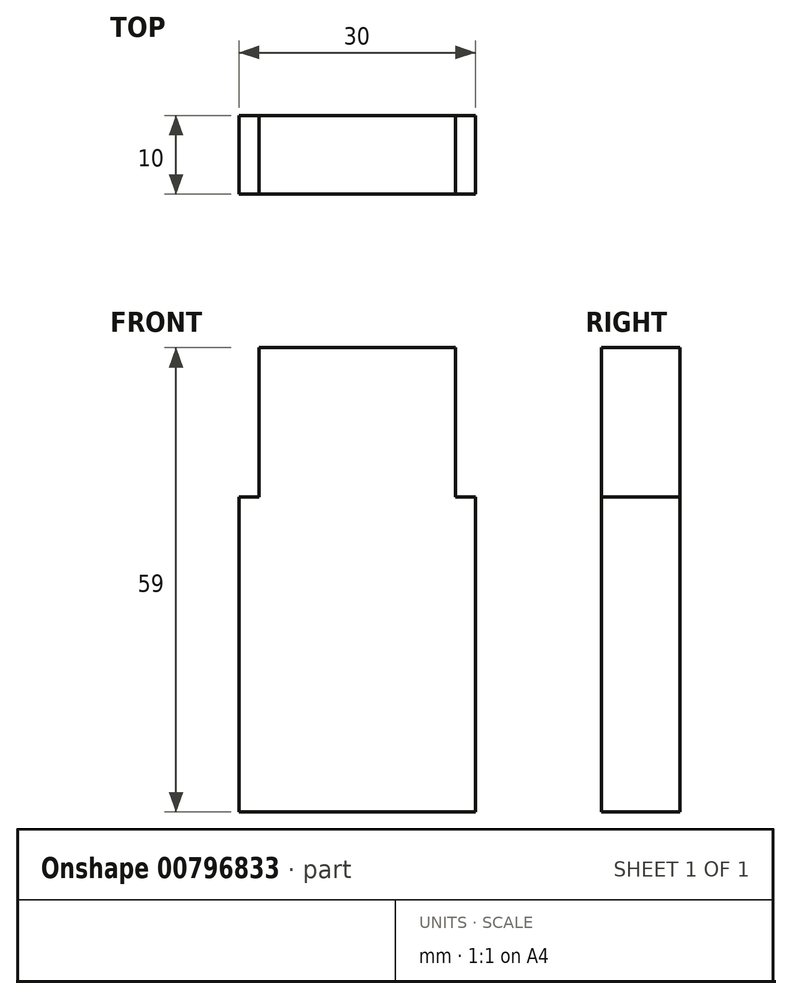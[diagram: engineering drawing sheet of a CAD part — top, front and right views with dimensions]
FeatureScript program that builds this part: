
annotation { "Feature Type Name" : "Feature", "Feature Type Description" : "" }
export const myFeature = defineFeature(function(context is Context, id is Id, definition is map)
    precondition{}
    {
        {
            var Q0;
            Q0=qCreatedBy(makeId("Top.planeOp"),FACE);
            var sketch = newSketch(context, id + "F0", { "sketchPlane" : qUnion([Q0])});
            skLineSegment(sketch, "E0.bottom", {"start": v(15, -5) * mm, "end": v(-15, -5) * mm});
            skLineSegment(sketch, "E0.top", {"start": v(15, 5) * mm, "end": v(-15, 5) * mm});
            skLineSegment(sketch, "E0.left", {"start": v(15, -5) * mm, "end": v(15, 5) * mm});
            skLineSegment(sketch, "E0.right", {"start": v(-15, -5) * mm, "end": v(-15, 5) * mm});
            skPoint(sketch, "E0.middle", {"position": v(0, 0) * mm});
            skSolve(sketch);
        }
        {
            var Q0;
            Q0=makeQuery(id+"F0.imprint","IMPRINT",FACE,{"disambiguationData":[TD([[makeQuery(id+"F0.imprint","IMPRINT",EDGE,{"derivedFrom":sQuery(id+"F0.wireOp",EDGE,"E0.bottom")}),-1.0]])]});
            extrude(context, id + "F1", {"entities" : qUnion([Q0]), "depth" : 40 * mm, "offsetDistance" : 25 * mm});
        }
        {
            var Q0;
            Q0=makeQuery(id+"F1.opExtrude","CAP_FACE",FACE,{"disambiguationData":[OSD([sQuery(id+"F0.wireOp",EDGE,"E0.bottom"),sQuery(id+"F0.wireOp",EDGE,"E0.top"),sQuery(id+"F0.wireOp",EDGE,"E0.left"),sQuery(id+"F0.wireOp",EDGE,"E0.right")])],"isStart":false});
            var sketch = newSketch(context, id + "F2", { "sketchPlane" : qUnion([Q0])});
            skLineSegment(sketch, "E1.bottom", {"start": v(12.5, -5) * mm, "end": v(-12.5, -5) * mm});
            skLineSegment(sketch, "E1.top", {"start": v(12.5, 5) * mm, "end": v(-12.5, 5) * mm});
            skLineSegment(sketch, "E1.left", {"start": v(12.5, -5) * mm, "end": v(12.5, 5) * mm});
            skLineSegment(sketch, "E1.right", {"start": v(-12.5, -5) * mm, "end": v(-12.5, 5) * mm});
            skPoint(sketch, "E1.middle", {"position": v(0, 0) * mm});
            skSolve(sketch);
        }
        {
            var Q0;
            Q0=makeQuery(id+"F2.imprint","IMPRINT",FACE,{"disambiguationData":[TD([[makeQuery(id+"F2.imprint","IMPRINT",EDGE,{"derivedFrom":sQuery(id+"F2.wireOp",EDGE,"E1.bottom")}),-1.0]])]});
            extrude(context, id + "F3", {"entities" : qUnion([Q0]), "operationType" : NewBodyOperationType.ADD, "depth" : 12 * mm, "offsetDistance" : 25 * mm});
        }
        {
            var Q0;
            Q0=makeQuery(id+"F3.opExtrude","CAP_FACE",FACE,{"disambiguationData":[OSD([sQuery(id+"F2.wireOp",EDGE,"E1.bottom"),sQuery(id+"F2.wireOp",EDGE,"E1.top"),sQuery(id+"F2.wireOp",EDGE,"E1.left"),sQuery(id+"F2.wireOp",EDGE,"E1.right")])],"isStart":false});
            var sketch = newSketch(context, id + "F4", { "sketchPlane" : qUnion([Q0])});
            skLineSegment(sketch, "E2.bottom", {"start": v(12.5, -5) * mm, "end": v(-12.5, -5) * mm});
            skLineSegment(sketch, "E2.top", {"start": v(12.5, 5) * mm, "end": v(-12.5, 5) * mm});
            skLineSegment(sketch, "E2.left", {"start": v(12.5, -5) * mm, "end": v(12.5, 5) * mm});
            skLineSegment(sketch, "E2.right", {"start": v(-12.5, -5) * mm, "end": v(-12.5, 5) * mm});
            skPoint(sketch, "E2.middle", {"position": v(0, 0) * mm});
            skSolve(sketch);
        }
        {
            var Q0;
            Q0=makeQuery(id+"F4.imprint","IMPRINT",FACE,{"disambiguationData":[TD([[makeQuery(id+"F4.imprint","IMPRINT",EDGE,{"derivedFrom":sQuery(id+"F4.wireOp",EDGE,"E2.bottom")}),-1.0]])]});
            extrude(context, id + "F5", {"entities" : qUnion([Q0]), "operationType" : NewBodyOperationType.ADD, "depth" : 7 * mm, "offsetDistance" : 25 * mm});
        }
    });
